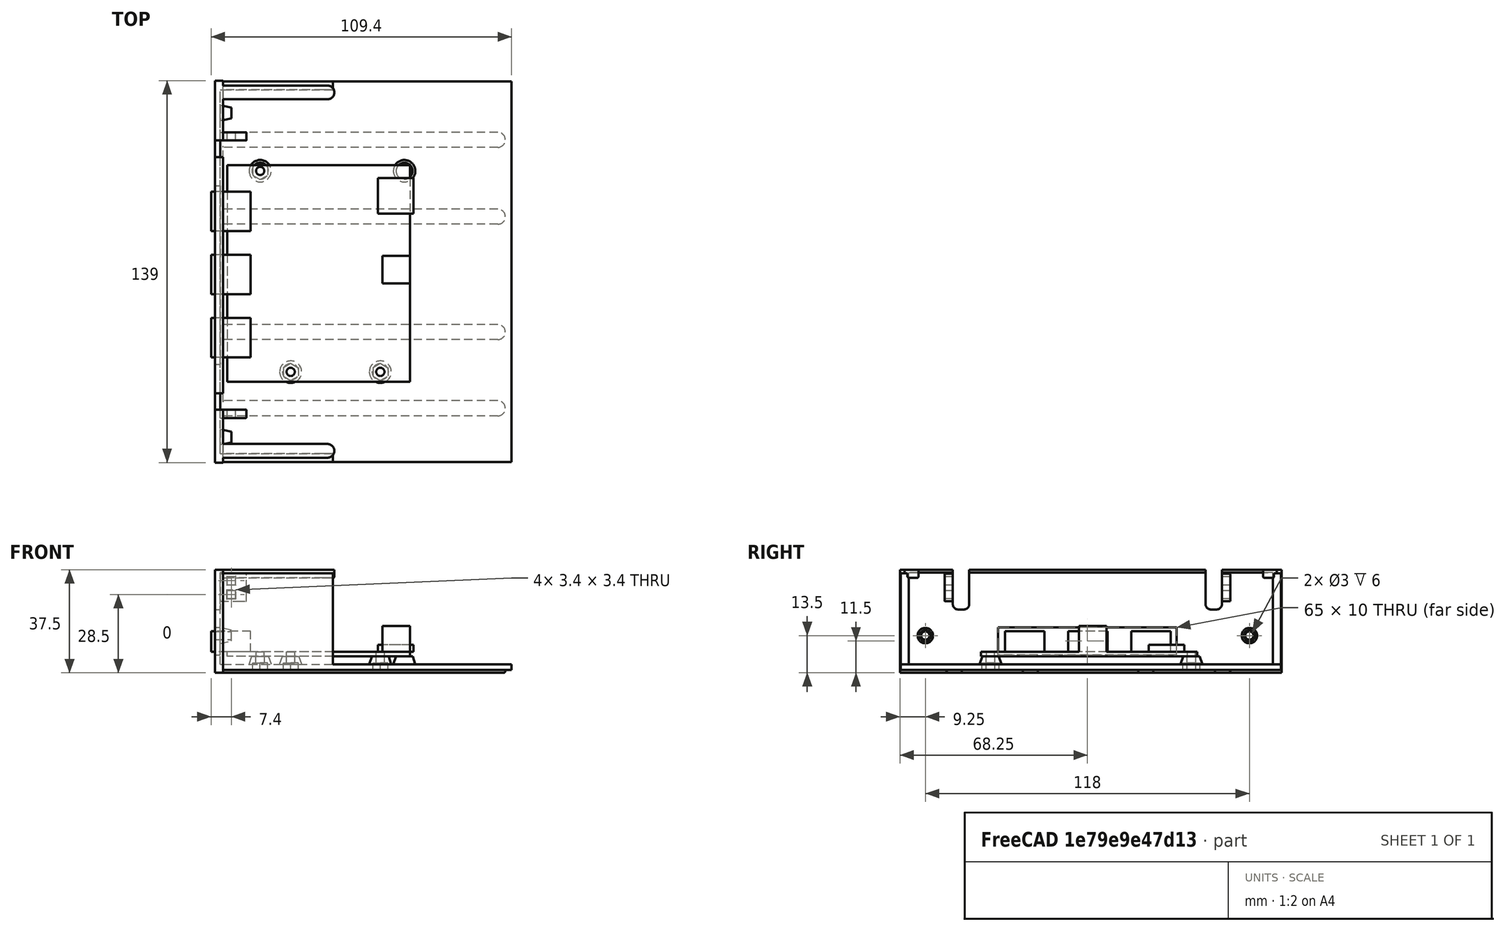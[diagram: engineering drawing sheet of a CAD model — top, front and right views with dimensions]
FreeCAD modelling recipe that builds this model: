
FCSTD DOCUMENT  (FreeCAD 0.19R24291 (Git))
Label: ykush3_tray
License: All rights reserved
LicenseURL: http://en.wikipedia.org/wiki/All_rights_reserved
objects: Part::Box×35, Part::MultiFuse×27, Part::Fillet×16, Part::Cylinder×14, Part::Cut×7, Part::Cone×6, Part::MultiCommon×3
note: 108 computed .brp shape members not serialized (recipe doc carries the construction recipe); baked Part::Feature solids carry a one-line shape summary decoded from their .brp

FEATURE [Part::Box] Box007  label="Cube007"
  AttacherType = Attacher::AttachEngine3D
  Height = 35.2
  Length = 40
  Placement = pos=(0,115.5,0) rot=(0,0,1;0rad)
  Width = 3
FEATURE [Part::Cylinder] Cylinder008
  Angle = 360
  AttacherType = Attacher::AttachEngine3D
  Height = 3
  Placement = pos=(38,2.5,-2) rot=(0,0,-1;0rad)
  Radius = 2.5
FEATURE [Part::Box] Box008  label="Cube008"
  AttacherType = Attacher::AttachEngine3D
  Height = 3
  Length = 38
  Placement = pos=(0,0,-2) rot=(0,0,1;0rad)
  Width = 5
FEATURE [Part::Fillet] Fillet008
  Base = -> Box008
  Edges = 2 edges r=0.5: [Edge9,Edge11]
FEATURE [Part::Cylinder] Cylinder009
  Angle = 360
  AttacherType = Attacher::AttachEngine3D
  Height = 3
  Placement = pos=(38,2.5,-2) rot=(0,0,-1;0rad)
  Radius = 2.5
FEATURE [Part::Fillet] Fillet011
  Base = -> Cylinder009
  Edges = 1 edges r=0.5: [Edge3]
FEATURE [Part::Box] Box009  label="Cube009"
  AttacherType = Attacher::AttachEngine3D
  Height = 3
  Length = 38
  Placement = pos=(0,0,-2) rot=(0,0,1;0rad)
  Width = 5
FEATURE [Part::Fillet] Fillet009
  Base = -> Cylinder008
  Edges = 1 edges r=0.5: [Edge3]
FEATURE [Part::MultiFuse] Fusion005
  Placement = pos=(0,-18.5,35.5) rot=(0,0,1;0rad)
  Shapes = -> [Fillet008,Fillet009]
FEATURE [Part::Fillet] Fillet010
  Base = -> Box009
  Edges = 2 edges r=0.5: [Edge9,Edge11]
FEATURE [Part::MultiFuse] Fusion006
  Placement = pos=(0,112,35.5) rot=(0,0,1;0rad)
  Shapes = -> [Fillet010,Fillet011]
FEATURE [Part::Box] Box006  label="Cube006"
  AttacherType = Attacher::AttachEngine3D
  Height = 35.2
  Length = 40
  Placement = pos=(0,-20,0) rot=(0,0,1;0rad)
  Width = 3
FEATURE [Part::MultiFuse] Fusion013  label="side"
  Shapes = -> [Fusion005,Fusion006,Box007,Box006]
FEATURE [Part::Cylinder] Cylinder005
  Angle = 360
  AttacherType = Attacher::AttachEngine3D
  Height = 3
  Placement = pos=(100,2.75,-2) rot=(0,0,-1;0rad)
  Radius = 2.75
FEATURE [Part::Fillet] Fillet003
  Base = -> Cylinder005
  Edges = 1 edges r=0.5: [Edge3]
FEATURE [Part::Cylinder] Cylinder004
  Angle = 360
  AttacherType = Attacher::AttachEngine3D
  Height = 3
  Placement = pos=(100,2.75,-2) rot=(0,0,-1;0rad)
  Radius = 2.75
FEATURE [Part::Fillet] Fillet001
  Base = -> Cylinder004
  Edges = 1 edges r=0.5: [Edge3]
FEATURE [Part::Cylinder] Cylinder006
  Angle = 360
  AttacherType = Attacher::AttachEngine3D
  Height = 3
  Placement = pos=(100,2.75,-2) rot=(0,0,-1;0rad)
  Radius = 2.75
FEATURE [Part::Box] Box004  label="Cube004"
  AttacherType = Attacher::AttachEngine3D
  Height = 3
  Length = 100
  Placement = pos=(0,0,-2) rot=(0,0,1;0rad)
  Width = 5.5
FEATURE [Part::Box] Box  label="Cube"
  AttacherType = Attacher::AttachEngine3D
  Height = 2
  Length = 105
  Placement = pos=(0,-20,0) rot=(0,0,1;0rad)
  Width = 138.5
FEATURE [Part::Fillet] Fillet005
  Base = -> Cylinder006
  Edges = 1 edges r=0.5: [Edge3]
FEATURE [Part::Cylinder] Cylinder007
  Angle = 360
  AttacherType = Attacher::AttachEngine3D
  Height = 3
  Placement = pos=(100,2.75,-2) rot=(0,0,-1;0rad)
  Radius = 2.75
FEATURE [Part::Fillet] Fillet007
  Base = -> Cylinder007
  Edges = 1 edges r=0.5: [Edge3]
FEATURE [Part::Box] Box005  label="Cube005"
  AttacherType = Attacher::AttachEngine3D
  Height = 3
  Length = 100
  Placement = pos=(0,0,-2) rot=(0,0,1;0rad)
  Width = 5.5
FEATURE [Part::Fillet] Fillet006
  Base = -> Box005
  Edges = 2 edges r=0.5: [Edge9,Edge11]
FEATURE [Part::MultiFuse] Fusion004
  Placement = pos=(0,24.5,1) rot=(0,0,1;0rad)
  Shapes = -> [Fillet006,Fillet007]
FEATURE [Part::Box] Box003  label="Cube003"
  AttacherType = Attacher::AttachEngine3D
  Height = 3
  Length = 100
  Placement = pos=(0,0,-2) rot=(0,0,1;0rad)
  Width = 5.5
FEATURE [Part::Fillet] Fillet002
  Base = -> Box003
  Edges = 2 edges r=0.5: [Edge9,Edge11]
FEATURE [Part::MultiFuse] Fusion002
  Placement = pos=(0,94.5,1) rot=(0,0,1;0rad)
  Shapes = -> [Fillet002,Fillet003]
FEATURE [Part::Box] Box002  label="Cube002"
  AttacherType = Attacher::AttachEngine3D
  Height = 3
  Length = 100
  Placement = pos=(0,0,-2) rot=(0,0,1;0rad)
  Width = 5.5
FEATURE [Part::Fillet] Fillet
  Base = -> Box002
  Edges = 2 edges r=0.5: [Edge9,Edge11]
FEATURE [Part::MultiFuse] Fusion001
  Placement = pos=(0,-3.25,1) rot=(0,0,1;0rad)
  Shapes = -> [Fillet,Fillet001]
FEATURE [Part::Fillet] Fillet004
  Base = -> Box004
  Edges = 2 edges r=0.5: [Edge9,Edge11]
FEATURE [Part::MultiFuse] Fusion003
  Placement = pos=(0,66.5,1) rot=(0,0,1;0rad)
  Shapes = -> [Fillet004,Fillet005]
FEATURE [Part::Box] Box001  label="Cube001"
  AttacherType = Attacher::AttachEngine3D
  Height = 37.5
  Length = 3
  Placement = pos=(-5,-19.25,-1) rot=(0,0,1;0rad)
  Width = 139
FEATURE [Part::Box] Box017  label="Cube017"
  AttacherType = Attacher::AttachEngine3D
  Height = 33.5
  Length = 4
  Placement = pos=(-3,-16,2) rot=(0,0,1;0rad)
  Width = 132.5
FEATURE [Part::Cut] Cut  label="Face_plate_full"
  Base = -> Box001
  Placement = pos=(2,0,0) rot=(0,0,1;0rad)
  Tool = -> Box017
FEATURE [Part::Box] Box031  label="Cube031"
  AttacherType = Attacher::AttachEngine3D
  Height = 10
  Length = 10
  Placement = pos=(-5,16.5,5.5) rot=(0,0,1;0rad)
  Width = 65
FEATURE [Part::Box] Box045  label="Cube044"
  AttacherType = Attacher::AttachEngine3D
  Height = 10
  Length = 10
  Placement = pos=(0,10,26) rot=(0,0,1;0rad)
  Width = 3
FEATURE [Part::Box] Box046  label="Cube045"
  AttacherType = Attacher::AttachEngine3D
  Height = 3
  Length = 3
  Placement = pos=(3,10,27) rot=(0,0,1;0rad)
  Width = 3
FEATURE [Part::Box] Box047  label="Cube046"
  AttacherType = Attacher::AttachEngine3D
  Height = 3
  Length = 3
  Placement = pos=(3,10,32) rot=(0,0,1;0rad)
  Width = 3
FEATURE [Part::MultiFuse] Fusion025
  Shapes = -> [Box046,Box047]
FEATURE [Part::Cut] Cut010
  Base = -> Box045
  Tool = -> Fusion025
FEATURE [Part::Fillet] Fillet022  label="zip ties holder"
  Base = -> Cut010
  Edges = 22 edges r=0.2: [Edge5,Edge6,Edge7,Edge8,Edge9,Edge10,Edge11,Edge12,Edge13,Edge14,Edge15,Edge16,Edge19,Edge20,Edge21,Edge22,Edge23,Edge24,Edge25,Edge26,Edge27,Edge28]
  Placement = pos=(-1,-13,-1) rot=(0,0,1;0rad)
FEATURE [Part::Box] Box048  label="Cube047"
  AttacherType = Attacher::AttachEngine3D
  Height = 10
  Length = 10
  Placement = pos=(0,10,26) rot=(0,0,1;0rad)
  Width = 3
FEATURE [Part::Box] Box049  label="Cube048"
  AttacherType = Attacher::AttachEngine3D
  Height = 3
  Length = 3
  Placement = pos=(3,10,27) rot=(0,0,1;0rad)
  Width = 3
FEATURE [Part::Box] Box050  label="Cube049"
  AttacherType = Attacher::AttachEngine3D
  Height = 3
  Length = 3
  Placement = pos=(3,10,32) rot=(0,0,1;0rad)
  Width = 3
FEATURE [Part::MultiFuse] Fusion026
  Shapes = -> [Box049,Box050]
FEATURE [Part::Cut] Cut011
  Base = -> Box048
  Tool = -> Fusion026
FEATURE [Part::Fillet] Fillet023  label="zip ties holder001"
  Base = -> Cut011
  Edges = 22 edges r=0.2: [Edge5,Edge6,Edge7,Edge8,Edge9,Edge10,Edge11,Edge12,Edge13,Edge14,Edge15,Edge16,Edge19,Edge20,Edge21,Edge22,Edge23,Edge24,Edge25,Edge26,Edge27,Edge28]
  Placement = pos=(-1,88,-1) rot=(0,0,1;0rad)
FEATURE [Part::MultiFuse] Fusion027  label="zip ties holders"
  Placement = pos=(-0.5,0,0) rot=(0,0,1;0rad)
  Shapes = -> [Fillet022,Fillet023]
FEATURE [Part::Cylinder] Cylinder016
  Angle = 360
  AttacherType = Attacher::AttachEngine3D
  Height = 10
  Placement = pos=(-5,-10,32.5) rot=(0,1,0;1.5708rad)
  Radius = 1.5
FEATURE [Part::Cylinder] Cylinder017
  Angle = 360
  AttacherType = Attacher::AttachEngine3D
  Height = 10
  Placement = pos=(-5,108,32.5) rot=(0,1,0;1.5708rad)
  Radius = 1.5
FEATURE [Part::MultiFuse] Fusion023
  Placement = pos=(0,0,-20) rot=(0,0,1;0rad)
  Shapes = -> [Cylinder016,Cylinder017]
FEATURE [Part::Cone] Cone006
  Angle = 360
  AttacherType = Attacher::AttachEngine3D
  Height = 5
  Placement = pos=(-1,-10,32.5) rot=(0,1,0;1.5708rad)
  Radius1 = 3
  Radius2 = 2
FEATURE [Part::Cone] Cone007
  Angle = 360
  AttacherType = Attacher::AttachEngine3D
  Height = 5
  Placement = pos=(-1,108,32.5) rot=(0,1,0;1.5708rad)
  Radius1 = 3
  Radius2 = 2
FEATURE [Part::MultiFuse] Fusion022
  Placement = pos=(-1,0,-20) rot=(0,0,1;0rad)
  Shapes = -> [Cone006,Cone007]
  expr: .Placement.Base.z = -20
FEATURE [Part::Box] Box018  label="Cube018"
  AttacherType = Attacher::AttachEngine3D
  Height = 15
  Length = 10
  Placement = pos=(0,0,16) rot=(0,0,1;0rad)
  Width = 6
FEATURE [Part::Fillet] Fillet012
  Base = -> Box018
  Edges = 2 edges r=2: [Edge9,Edge11]
  Placement = pos=(0,0,4) rot=(0,0,1;0rad)
FEATURE [Part::Box] Box020  label="Cube020"
  AttacherType = Attacher::AttachEngine3D
  Height = 15
  Length = 10
  Placement = pos=(0,0,16) rot=(0,0,1;0rad)
  Width = 6
FEATURE [Part::Fillet] Fillet014
  Base = -> Box020
  Edges = 2 edges r=2: [Edge9,Edge11]
  Placement = pos=(0,92,4) rot=(0,0,1;0rad)
FEATURE [Part::MultiFuse] Fusion
  Placement = pos=(-5,0,2) rot=(0,0,1;0rad)
  Shapes = -> [Fillet012,Fillet014]
FEATURE [Part::MultiFuse] Fusion028
  Shapes = -> [Fusion022,Fusion027,Cut]
FEATURE [Part::MultiFuse] Fusion029
  Shapes = -> [Fusion023,Fusion]
FEATURE [Part::Cut] Cut012
  Base = -> Fusion028
  Tool = -> Fusion029
FEATURE [Part::Cut] Cut013  label="face plate"
  Base = -> Cut012
  Placement = pos=(0,-1,0) rot=(0,0,1;0rad)
  Tool = -> Box031
FEATURE [Part::MultiFuse] Fusion030  label="ykush_tray_f"
  Shapes = -> [Fusion013,Cut013]
FEATURE [Part::Cone] Cone008  label="screws cones"
  Angle = 360
  AttacherType = Attacher::AttachEngine3D
  Height = 3
  Placement = pos=(-24.6,-11.75,2) rot=(0,0,1;0rad)
  Radius1 = 4
  Radius2 = 3
FEATURE [Part::Cone] Cone009  label="screws cones001"
  Angle = 360
  AttacherType = Attacher::AttachEngine3D
  Height = 3
  Placement = pos=(-57.24,-11.75,2) rot=(0,0,1;0rad)
  Radius1 = 4
  Radius2 = 3
FEATURE [Part::Cone] Cone010  label="screws cones002"
  Angle = 360
  AttacherType = Attacher::AttachEngine3D
  Height = 3
  Placement = pos=(-13.5,-84.9,2) rot=(0,0,1;0rad)
  Radius1 = 4
  Radius2 = 3
FEATURE [Part::Cone] Cone011  label="screws cones004"
  Angle = 360
  AttacherType = Attacher::AttachEngine3D
  Height = 3
  Placement = pos=(-66,-84.9,2) rot=(0,0,1;0rad)
  Radius1 = 4
  Radius2 = 3
FEATURE [Part::MultiFuse] Fusion039  label="screws cones003"
  Placement = pos=(0,1,0) rot=(0,0,1;3.14159rad)
  Shapes = -> [Cone008,Cone009,Cone010,Cone011]
FEATURE [Part::MultiFuse] Fusion007  label="Bottom"
  Shapes = -> [Box,Fusion001,Fusion002,Fusion003,Fusion004,Fusion039]
FEATURE [Part::Box] Box056  label="Cube055"
  AttacherType = Attacher::AttachEngine3D
  Height = 5
  Length = 5.45
  Placement = pos=(3.25,0,0) rot=(0,0,1;0rad)
  Width = 10
FEATURE [Part::Box] Box057  label="Cube056"
  AttacherType = Attacher::AttachEngine3D
  Height = 5
  Length = 5.45
  Placement = pos=(11.5,4,0) rot=(0,0,1;2.0944rad)
  Width = 10
FEATURE [Part::Box] Box058  label="Cube057"
  AttacherType = Attacher::AttachEngine3D
  Height = 5
  Length = 10
  Placement = pos=(0.55,4,0) rot=(0,0,-1;0.523599rad)
  Width = 5.45
FEATURE [Part::MultiCommon] Common004  label="M.25 nut004"
  Placement = pos=(-2,0,-1) rot=(0,0,1;0rad)
  Shapes = -> [Box056,Box058,Box057]
FEATURE [Part::Cylinder] Cylinder021
  Angle = 360
  AttacherType = Attacher::AttachEngine3D
  Height = 10
  Placement = pos=(4,4,-1) rot=(0,0,1;0rad)
  Radius = 1.55
FEATURE [Part::MultiFuse] Fusion035  label="screw_hole004"
  Placement = pos=(-28.6,-15.75,0) rot=(0,0,1;0rad)
  Shapes = -> [Cylinder021,Common004]
FEATURE [Part::Box] Box059  label="Cube058"
  AttacherType = Attacher::AttachEngine3D
  Height = 5
  Length = 5.45
  Placement = pos=(3.25,0,0) rot=(0,0,1;0rad)
  Width = 10
FEATURE [Part::Box] Box060  label="Cube059"
  AttacherType = Attacher::AttachEngine3D
  Height = 5
  Length = 5.45
  Placement = pos=(11.5,4,0) rot=(0,0,1;2.0944rad)
  Width = 10
FEATURE [Part::Cylinder] Cylinder022
  Angle = 360
  AttacherType = Attacher::AttachEngine3D
  Height = 10
  Placement = pos=(4,4,-1) rot=(0,0,1;0rad)
  Radius = 1.55
FEATURE [Part::Box] Box062  label="Cube061"
  AttacherType = Attacher::AttachEngine3D
  Height = 5
  Length = 5.45
  Placement = pos=(3.25,0,0) rot=(0,0,1;0rad)
  Width = 10
FEATURE [Part::Cylinder] Cylinder023
  Angle = 360
  AttacherType = Attacher::AttachEngine3D
  Height = 10
  Placement = pos=(4,4,-1) rot=(0,0,1;0rad)
  Radius = 1.55
FEATURE [Part::Box] Box063  label="Cube062"
  AttacherType = Attacher::AttachEngine3D
  Height = 5
  Length = 10
  Placement = pos=(0.55,4,0) rot=(0,0,-1;0.523599rad)
  Width = 5.45
FEATURE [Part::Box] Box064  label="Cube063"
  AttacherType = Attacher::AttachEngine3D
  Height = 5
  Length = 5.45
  Placement = pos=(11.5,4,0) rot=(0,0,1;2.0944rad)
  Width = 10
FEATURE [Part::MultiCommon] Common006  label="M.25 nut006"
  Placement = pos=(-2,0,-1) rot=(0,0,1;0rad)
  Shapes = -> [Box062,Box063,Box064]
FEATURE [Part::MultiFuse] Fusion037  label="screw_hole006"
  Placement = pos=(-17.5,-88.9,0) rot=(0,0,1;0rad)
  Shapes = -> [Cylinder023,Common006]
FEATURE [Part::Box] Box061  label="Cube060"
  AttacherType = Attacher::AttachEngine3D
  Height = 5
  Length = 10
  Placement = pos=(0.55,4,0) rot=(0,0,-1;0.523599rad)
  Width = 5.45
FEATURE [Part::MultiCommon] Common005  label="M.25 nut005"
  Placement = pos=(-2,0,-1) rot=(0,0,1;0rad)
  Shapes = -> [Box059,Box061,Box060]
FEATURE [Part::MultiFuse] Fusion036  label="screw_hole005"
  Placement = pos=(-61.25,-15.75,0) rot=(0,0,1;0rad)
  Shapes = -> [Cylinder022,Common005]
FEATURE [Part::MultiFuse] Fusion038  label="screws holes"
  Placement = pos=(0,1,-1.5) rot=(0,0,1;3.14159rad)
  Shapes = -> [Fusion035,Fusion036,Fusion037]
FEATURE [Part::Box] Box052  label="Cube051"
  AttacherType = Attacher::AttachEngine3D
  Height = 7.5
  Length = 14.4
  Placement = pos=(58,32.6,6.6) rot=(0,0,1;0rad)
  Width = 14.4
FEATURE [Part::Box] Box054  label="Cube053"
  AttacherType = Attacher::AttachEngine3D
  Height = 2.6
  Length = 12.9
  Placement = pos=(-1.3,4.7,6.6) rot=(0,0,1;0rad)
  Width = 12.9
FEATURE [Part::Box] Box055  label="Cube054"
  AttacherType = Attacher::AttachEngine3D
  Height = 10
  Length = 10
  Placement = pos=(0,33,6) rot=(0,0,1;0rad)
  Width = 10
FEATURE [Part::Box] Box051  label="Cube050"
  AttacherType = Attacher::AttachEngine3D
  Height = 7.5
  Length = 14.4
  Placement = pos=(58,9.6,6.6) rot=(0,0,1;0rad)
  Width = 14.4
FEATURE [Part::Box] Box053  label="Cube052"
  AttacherType = Attacher::AttachEngine3D
  Height = 7.5
  Length = 14.4
  Placement = pos=(58,55.6,6.6) rot=(0,0,1;0rad)
  Width = 14.4
FEATURE [Part::MultiFuse] Fusion032
  Shapes = -> [Box051,Box052,Box053]
FEATURE [Part::MultiFuse] Fusion033
  Shapes = -> [Box054,Box055,Fusion032]
FEATURE [Part::Cylinder] Cylinder020
  Angle = 360
  AttacherType = Attacher::AttachEngine3D
  Height = 10
  Placement = pos=(54.5,2.1,0) rot=(0,0,1;0rad)
  Radius = 1.5
FEATURE [Part::Cylinder] Cylinder018
  Angle = 360
  AttacherType = Attacher::AttachEngine3D
  Height = 10
  Placement = pos=(10.75,75.25,0) rot=(0,0,1;0rad)
  Radius = 1.5
FEATURE [Part::Cylinder] Cylinder019
  Angle = 360
  AttacherType = Attacher::AttachEngine3D
  Height = 10
  Placement = pos=(43.4,75.25,0) rot=(0,0,1;0rad)
  Radius = 1.5
FEATURE [Part::MultiFuse] Fusion031
  Shapes = -> [Cylinder018,Cylinder019,Cylinder020]
FEATURE [Part::Box] Box065  label="ykush3_board"
  AttacherType = Attacher::AttachEngine3D
  Height = 1.6
  Length = 66.5
  Width = 78.8
FEATURE [Part::Cut] Cut014
  Base = -> Box065
  Placement = pos=(0,0,5) rot=(0,0,1;0rad)
  Tool = -> Fusion031
FEATURE [Part::MultiFuse] Fusion034  label="ykush3_board001"
  Placement = pos=(68,88,0) rot=(0,0,1;3.14159rad)
  Shapes = -> [Cut014,Fusion033]
FEATURE [Part::Cut] Cut015  label="bottom"
  Base = -> Fusion007
  Tool = -> Fusion038
FEATURE [Part::MultiFuse] Fusion040  label="ykush3_tray_final"
  Shapes = -> [Fusion030,Cut015]
